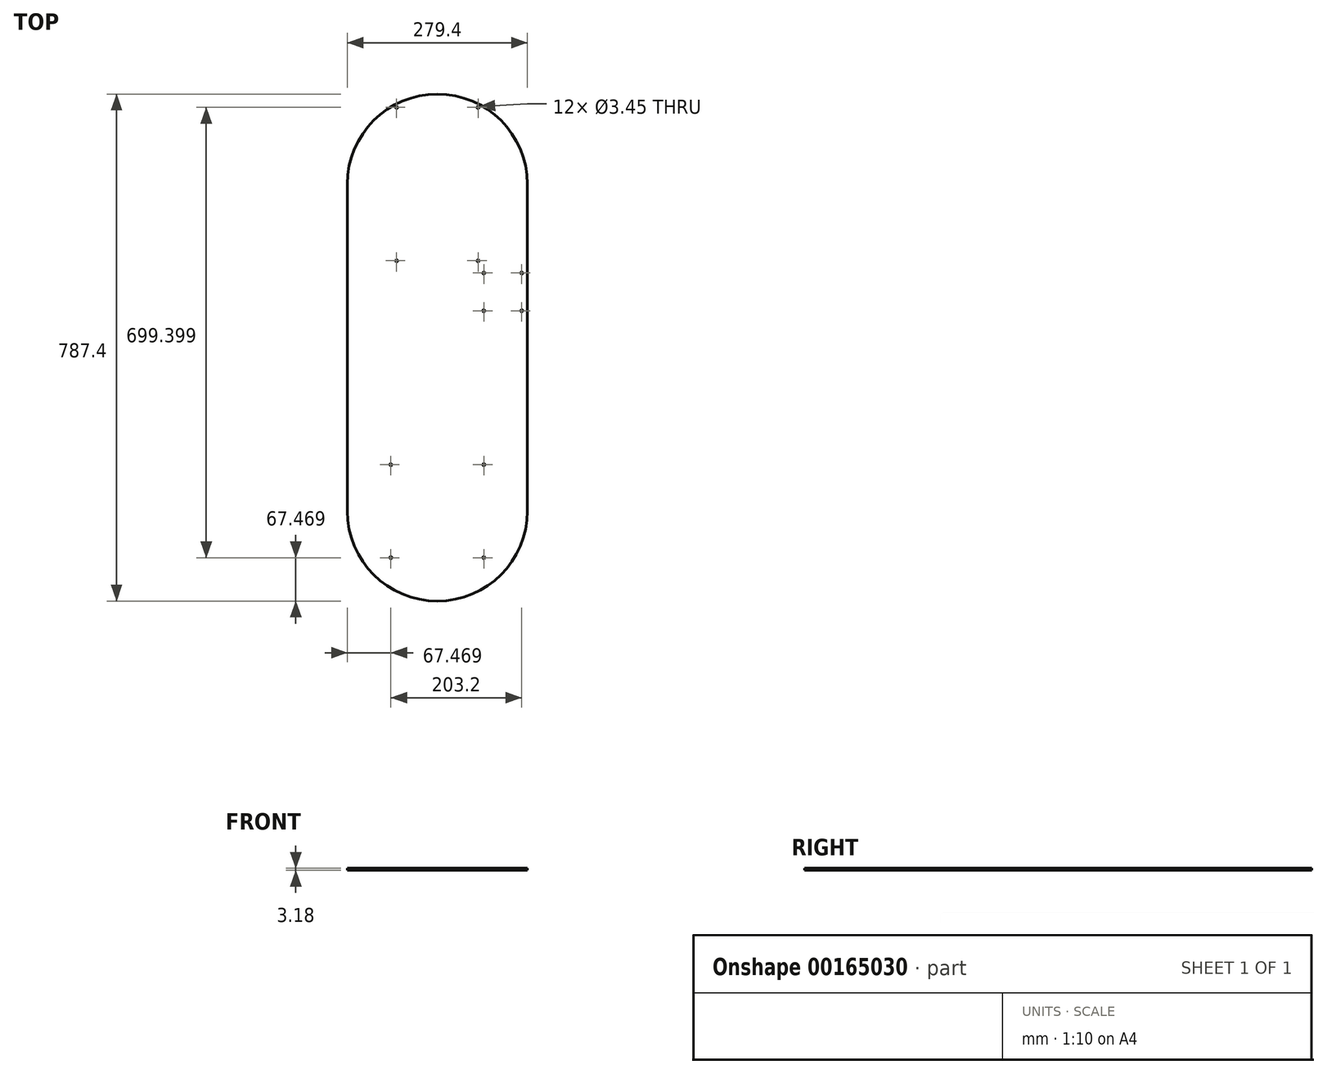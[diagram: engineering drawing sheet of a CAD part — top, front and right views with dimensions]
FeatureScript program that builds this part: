
annotation { "Feature Type Name" : "Feature", "Feature Type Description" : "" }
export const myFeature = defineFeature(function(context is Context, id is Id, definition is map)
    precondition{}
    {
        {
            var Q0;
            Q0=qCreatedBy(makeId("Top.planeOp"),FACE);
            var sketch = newSketch(context, id + "F0", { "sketchPlane" : qUnion([Q0])});
            skLineSegment(sketch, "E0.bottom", {"start": v(0, 0) * mm, "end": v(279.4, 0) * mm, "construction": true});
            skLineSegment(sketch, "E0.top", {"start": v(0, -508) * mm, "end": v(279.4, -508) * mm, "construction": true});
            skLineSegment(sketch, "E0.left", {"start": v(0, 0) * mm, "end": v(0, -508) * mm});
            skLineSegment(sketch, "E0.right", {"start": v(279.4, 0) * mm, "end": v(279.4, -508) * mm});
            skArc(sketch, "E1", {"start": v(279.4, 0) * mm, "mid": v(139.7, 139.7) * mm, "end": v(0, 0) * mm});
            skArc(sketch, "E2", {"start": v(0, -508) * mm, "mid": v(139.7, -647.7) * mm, "end": v(279.4, -508) * mm});
            skLineSegment(sketch, "E3", {"start": v(139.7, 0) * mm, "end": v(139.7, -119.17) * mm, "construction": true});
            skLineSegment(sketch, "E4", {"start": v(139.7, 0) * mm, "end": v(139.7, 119.17) * mm, "construction": true});
            skLineSegment(sketch, "E5", {"start": v(76.4, 119.17) * mm, "end": v(203, 119.17) * mm, "construction": true});
            skLineSegment(sketch, "E6", {"start": v(203, 119.17) * mm, "end": v(139.7, 0) * mm, "construction": true});
            skLineSegment(sketch, "E7", {"start": v(139.7, 0) * mm, "end": v(76.4, 119.17) * mm, "construction": true});
            skLineSegment(sketch, "E8", {"start": v(76.4, -119.17) * mm, "end": v(203, -119.17) * mm, "construction": true});
            skLineSegment(sketch, "E9", {"start": v(139.7, -119.17) * mm, "end": v(139.7, -167.48) * mm, "construction": true});
            skLineSegment(sketch, "E10", {"start": v(139.7, -167.48) * mm, "end": v(241.3, -167.48) * mm, "construction": true});
            skLineSegment(sketch, "E11.bottom", {"start": v(270.67, -138.11) * mm, "end": v(211.93, -138.11) * mm, "construction": true});
            skLineSegment(sketch, "E11.top", {"start": v(270.67, -196.85) * mm, "end": v(211.93, -196.85) * mm, "construction": true});
            skLineSegment(sketch, "E11.left", {"start": v(270.67, -138.11) * mm, "end": v(270.67, -196.85) * mm, "construction": true});
            skLineSegment(sketch, "E11.right", {"start": v(211.93, -138.11) * mm, "end": v(211.93, -196.85) * mm, "construction": true});
            skPoint(sketch, "E11.middle", {"position": v(241.3, -167.48) * mm});
            skLineSegment(sketch, "E12.bottom", {"start": v(211.93, -435.77) * mm, "end": v(67.47, -435.77) * mm, "construction": true});
            skLineSegment(sketch, "E12.top", {"start": v(211.93, -580.23) * mm, "end": v(67.47, -580.23) * mm, "construction": true});
            skLineSegment(sketch, "E12.left", {"start": v(211.93, -435.77) * mm, "end": v(211.93, -580.23) * mm, "construction": true});
            skLineSegment(sketch, "E12.right", {"start": v(67.47, -435.77) * mm, "end": v(67.47, -580.23) * mm, "construction": true});
            skCircle(sketch, "E13", {"center": v(67.47, -435.77) * mm, "radius": 1.73 * mm});
            skCircle(sketch, "E14", {"center": v(211.93, -435.77) * mm, "radius": 1.73 * mm});
            skCircle(sketch, "E15", {"center": v(67.47, -580.23) * mm, "radius": 1.73 * mm});
            skCircle(sketch, "E16", {"center": v(211.93, -580.23) * mm, "radius": 1.73 * mm});
            skCircle(sketch, "E17", {"center": v(211.93, -138.11) * mm, "radius": 1.73 * mm});
            skCircle(sketch, "E18", {"center": v(211.93, -196.85) * mm, "radius": 1.73 * mm});
            skCircle(sketch, "E19", {"center": v(270.67, -196.85) * mm, "radius": 1.73 * mm});
            skCircle(sketch, "E20", {"center": v(270.67, -138.11) * mm, "radius": 1.73 * mm});
            skCircle(sketch, "E21", {"center": v(76.4, -119.17) * mm, "radius": 1.73 * mm});
            skCircle(sketch, "E22", {"center": v(203, -119.17) * mm, "radius": 1.73 * mm});
            skCircle(sketch, "E23", {"center": v(203, 119.17) * mm, "radius": 1.73 * mm});
            skCircle(sketch, "E24", {"center": v(76.4, 119.17) * mm, "radius": 1.73 * mm});
            skSolve(sketch);
        }
        {
            var Q0;
            Q0 = qSketchRegion(id + "F0", true);
            extrude(context, id + "F1", {"entities" : qUnion([Q0]), "depth" : 3.17 * mm});
        }
    });
